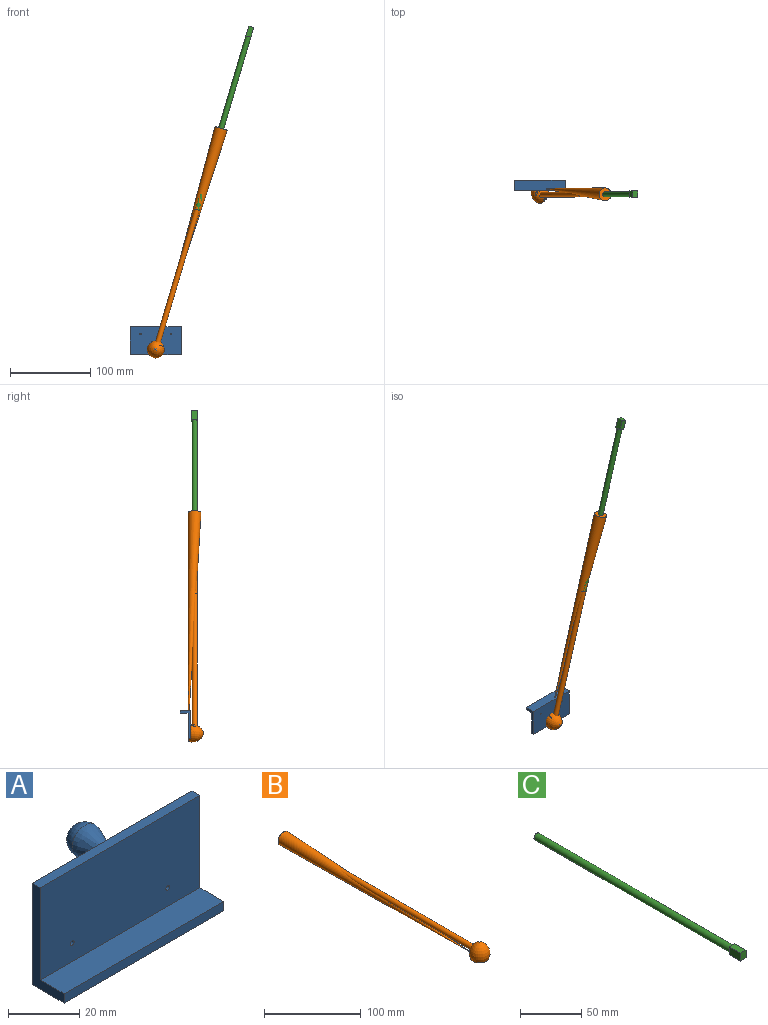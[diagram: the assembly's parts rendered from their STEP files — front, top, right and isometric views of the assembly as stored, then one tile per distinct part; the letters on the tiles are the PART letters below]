
ASSEMBLY  parts=3 mates=2
PART A: 12 faces, bbox 63.5x28.6x34.9 mm
  f0: plane 34.93x12.7mm, normal (-1,0,0), area 141.1mm2, adj f1,f3,f4,f5,f6,f7
  f1: plane 63.5x3.18mm, normal (0,-1,0), area 201.6mm2, adj f0,f2,f4,f5
  f2: plane 34.93x12.7mm, normal (1,0,0), area 141.1mm2, adj f1,f3,f4,f5,f6,f7
  f3: plane 63.5x34.93mm, normal (0,1,0), area 2173.3mm2, adj f0,f2,f5,f7,f9,f10,f11
  f4: plane 63.5x9.53mm, normal (0,0,1), area 604.8mm2, adj f0,f1,f2,f6
  f5: plane 63.5x12.7mm, normal (0,0,-1), area 806.4mm2, adj f0,f1,f2,f3
  f6: plane 63.5x31.75mm, normal (0,-1,0), area 2012.2mm2, adj f0,f2,f4,f7,f10,f11
  f7: plane 63.5x3.18mm, normal (0,0,1), area 201.6mm2, adj f0,f2,f3,f6
  f8: revolved ~10.3x10.3mm, area 167mm2, adj f9
  f9: revolved ~10.72x10.3mm, area 263.6mm2, adj f3,f8
  f10: cylinder r=0.79mm len=3.18mm, axis (0,-1,0), area 15.8mm2, adj f3,f6
  f11: cylinder r=0.79mm len=3.18mm, axis (0,-1,0), area 15.8mm2, adj f3,f6
PART B: 7 faces, bbox 57.2x335.1x54 mm
  f0: plane 57.15x57.15mm, normal (0,0,-1), area 285mm2, adj f1
  f1: revolved ~9.55x9.53mm, area 0mm2, adj f0
  f2: revolved ~16.43x15.88mm, area 233.9mm2, adj f3
  f3: cylinder r=7.94mm len=281.38mm, axis (0,-1,0), area 13966.4mm2, adj f2,f4
  f4: plane 15.88x15.88mm, normal (0,-1,0), area 166.3mm2, adj f3,f5
  f5: cylinder r=3.17mm len=279.4mm, axis (0,1,0), area 5573.8mm2, adj f4,f6
  f6: plane 6.35x6.35mm, normal (0,-1,0), area 31.7mm2, adj f5
PART C: 9 faces, bbox 6.4x238.1x7.9 mm
  f0: cylinder r=3.17mm len=225.43mm, axis (0,1,0), area 4497mm2, adj f1,f2,f3
  f1: plane 6.35x6.35mm, normal (0,1,0), area 31.7mm2, adj f0
  f2: plane 6.35x3.97mm, normal (0,1,0), area 9.4mm2, adj f0,f4,f6,f8
  f3: plane 6.35x3.97mm, normal (0,1,0), area 9.4mm2, adj f0,f4,f6,f7
  f4: plane 12.7x7.94mm, normal (-1,0,0), area 100.8mm2, adj f2,f3,f5,f7,f8
  f5: plane 7.94x6.35mm, normal (0,-1,0), area 50.4mm2, adj f4,f6,f7,f8
  f6: plane 12.7x7.94mm, normal (1,0,0), area 100.8mm2, adj f2,f3,f5,f7,f8
  f7: plane 12.7x6.35mm, normal (0,0,1), area 80.6mm2, adj f3,f4,f5,f6
  f8: plane 12.7x6.35mm, normal (0,0,-1), area 80.6mm2, adj f2,f4,f5,f6
PLACE A rot(axis=(1,0,0),180deg) t=(0,-11.92,0)mm
PLACE B rot(axis=(0.98,0.14,-0.14),91.2deg) t=(0,-3.43,-28.58)mm
PLACE C rot(axis=(-0.98,0.14,0.14),91.2deg) t=(115.45,-11.37,361.78)mm
MATE cylindrical B.f3 <-> C.f0  axis (-0.28,0,-0.96) through (81.52,-11.37,247.06)mm
MATE revolute B.f1 <-> A.f8  axis (0,1,0) through (0,-22.48,-28.58)mm
